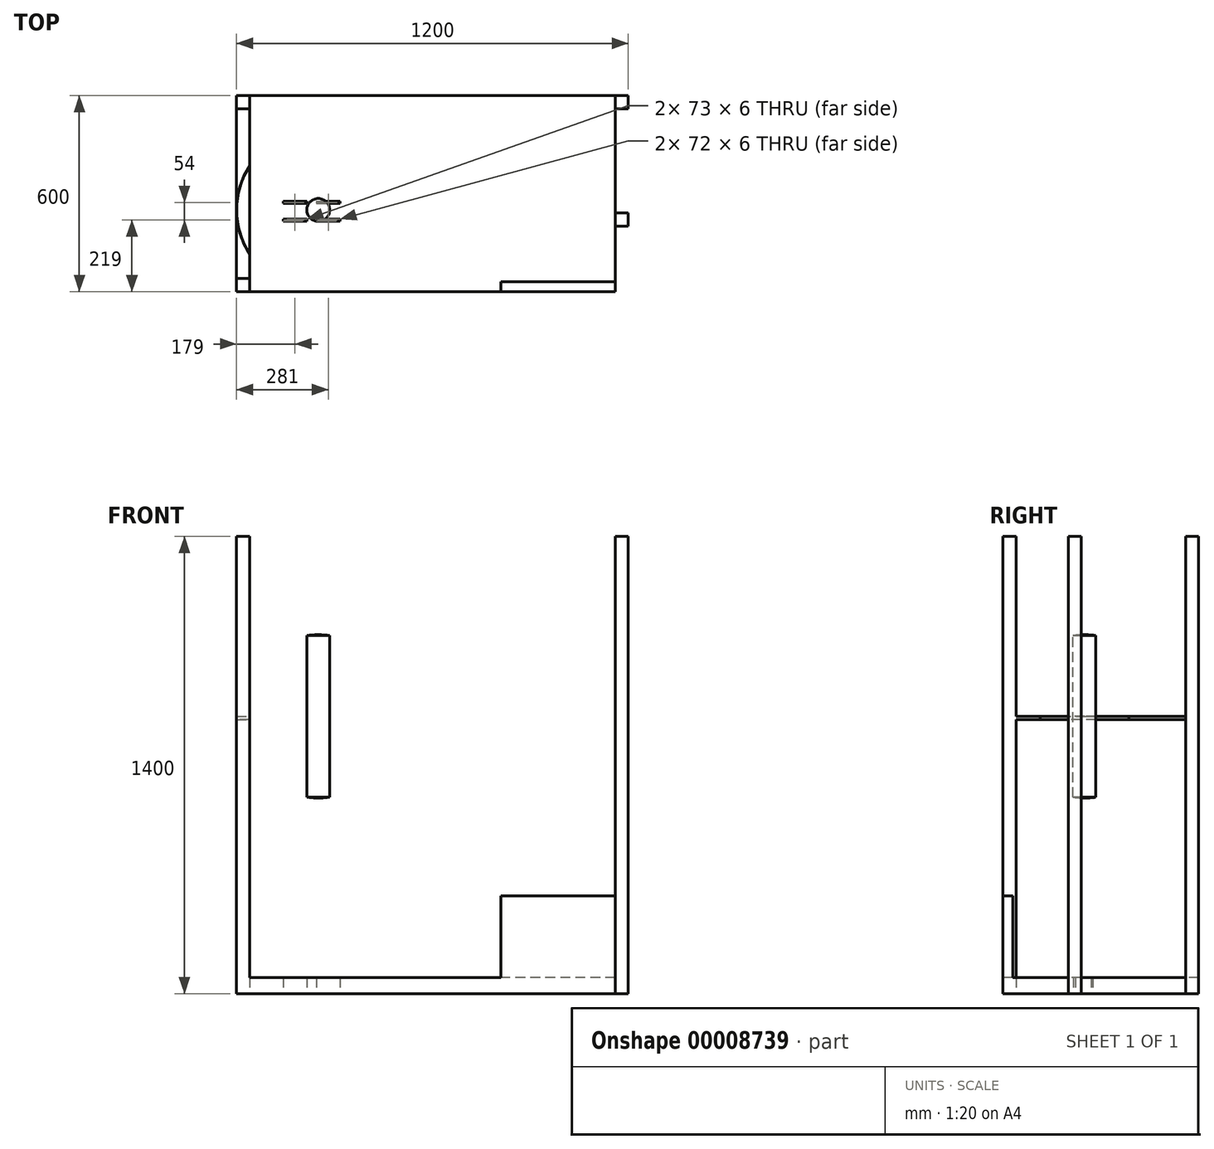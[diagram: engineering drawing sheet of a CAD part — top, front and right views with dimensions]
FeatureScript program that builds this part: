
annotation { "Feature Type Name" : "Feature", "Feature Type Description" : "" }
export const myFeature = defineFeature(function(context is Context, id is Id, definition is map)
    precondition{}
    {
        {
            var Q0;
            Q0=qCreatedBy(makeId("Top.planeOp"),FACE);
            var sketch = newSketch(context, id + "F0", { "sketchPlane" : qUnion([Q0])});
            skLineSegment(sketch, "E0.bottom", {"start": v(-250, 340) * mm, "end": v(870, 340) * mm});
            skLineSegment(sketch, "E0.top", {"start": v(-250, -260) * mm, "end": v(870, -260) * mm});
            skLineSegment(sketch, "E0.left", {"start": v(-250, 340) * mm, "end": v(-250, -260) * mm});
            skLineSegment(sketch, "E0.right", {"start": v(870, 340) * mm, "end": v(870, -260) * mm});
            skCircle(sketch, "E1", {"center": v(-40, 0) * mm, "radius": 250 * mm, "construction": true});
            skCircle(sketch, "E2", {"center": v(-40, 0) * mm, "radius": 30.5 * mm, "construction": true});
            skLineSegment(sketch, "E3", {"start": v(-250, 340) * mm, "end": v(870, -260) * mm, "construction": true});
            skLineSegment(sketch, "E4.left", {"start": v(-147.5, 16) * mm, "end": v(-147.5, 10) * mm});
            skLineSegment(sketch, "E4.right", {"start": v(-74.5, 16) * mm, "end": v(-74.5, 10) * mm});
            skLineSegment(sketch, "E5.top", {"start": v(-147.5, -44) * mm, "end": v(-74.5, -44) * mm});
            skLineSegment(sketch, "E5.left", {"start": v(-147.5, -38) * mm, "end": v(-147.5, -44) * mm});
            skLineSegment(sketch, "E5.right", {"start": v(-74.5, -38) * mm, "end": v(-74.5, -44) * mm});
            skLineSegment(sketch, "E6.bottom", {"start": v(-45, -38) * mm, "end": v(27, -38) * mm});
            skLineSegment(sketch, "E6.top", {"start": v(-45, -44) * mm, "end": v(27, -44) * mm});
            skLineSegment(sketch, "E6.left", {"start": v(-45, -38) * mm, "end": v(-45, -44) * mm});
            skLineSegment(sketch, "E6.right", {"start": v(27, -38) * mm, "end": v(27, -44) * mm});
            skLineSegment(sketch, "E7", {"start": v(-147.5, 16) * mm, "end": v(-74.5, 16) * mm});
            skLineSegment(sketch, "E8", {"start": v(-74.5, 10) * mm, "end": v(-147.5, 10) * mm});
            skLineSegment(sketch, "E9", {"start": v(-74.5, -38) * mm, "end": v(-147.5, -38) * mm});
            skLineSegment(sketch, "E10.bottom", {"start": v(-45, 16) * mm, "end": v(27, 16) * mm});
            skLineSegment(sketch, "E10.top", {"start": v(-45, 10) * mm, "end": v(27, 10) * mm});
            skLineSegment(sketch, "E10.left", {"start": v(-45, 16) * mm, "end": v(-45, 10) * mm});
            skLineSegment(sketch, "E10.right", {"start": v(27, 16) * mm, "end": v(27, 10) * mm});
            skLineSegment(sketch, "E11.bottom", {"start": v(870, -260) * mm, "end": v(520, -260) * mm, "construction": true});
            skLineSegment(sketch, "E11.top", {"start": v(870, -225) * mm, "end": v(520, -225) * mm, "construction": true});
            skLineSegment(sketch, "E11.left", {"start": v(870, -260) * mm, "end": v(870, -225) * mm, "construction": true});
            skLineSegment(sketch, "E11.right", {"start": v(520, -260) * mm, "end": v(520, -225) * mm, "construction": true});
            skSolve(sketch);
        }
        {
            var Q0;
            Q0 = qSketchRegion(id + "F0", true);
            extrude(context, id + "F1", {"entities" : qUnion([Q0]), "depth" : 49 * mm});
        }
        {
            var Q0;
            Q0=makeQuery(id+"F1.opExtrude","SWEPT_FACE",FACE,{"disambiguationData":[OSD([sQuery(id+"F0.wireOp",EDGE,"E0.top")])]});
            cPlane(context, id + "F2", {"entities" : qUnion([Q0]), "cplaneType" : CPlaneType.OFFSET, "offset" : 250 * mm, "oppositeDirection" : true, "width" : 150 * mm, "height" : 150 * mm});
        }
        {
            var Q0;
            Q0=makeQuery(id+"F1.opExtrude","CAP_FACE",FACE,{"disambiguationData":[OSD([sQuery(id+"F0.wireOp",EDGE,"E0.bottom"),sQuery(id+"F0.wireOp",EDGE,"E0.top"),sQuery(id+"F0.wireOp",EDGE,"E0.left"),sQuery(id+"F0.wireOp",EDGE,"E0.right"),sQuery(id+"F0.wireOp",EDGE,"E4.left"),sQuery(id+"F0.wireOp",EDGE,"E4.right"),sQuery(id+"F0.wireOp",EDGE,"E5.top"),sQuery(id+"F0.wireOp",EDGE,"E5.left"),sQuery(id+"F0.wireOp",EDGE,"E5.right"),sQuery(id+"F0.wireOp",EDGE,"E6.bottom"),sQuery(id+"F0.wireOp",EDGE,"E6.top"),sQuery(id+"F0.wireOp",EDGE,"E6.left"),sQuery(id+"F0.wireOp",EDGE,"E6.right"),sQuery(id+"F0.wireOp",EDGE,"E7"),sQuery(id+"F0.wireOp",EDGE,"E8"),sQuery(id+"F0.wireOp",EDGE,"E9"),sQuery(id+"F0.wireOp",EDGE,"E10.bottom"),sQuery(id+"F0.wireOp",EDGE,"E10.top"),sQuery(id+"F0.wireOp",EDGE,"E10.left"),sQuery(id+"F0.wireOp",EDGE,"E10.right"),sQuery(id+"F0.wireOp",EDGE,"473c598b-218d-4424-aa93-7a4d167d4974.bottom"),sQuery(id+"F0.wireOp",EDGE,"473c598b-218d-4424-aa93-7a4d167d4974.top"),sQuery(id+"F0.wireOp",EDGE,"473c598b-218d-4424-aa93-7a4d167d4974.left"),sQuery(id+"F0.wireOp",EDGE,"473c598b-218d-4424-aa93-7a4d167d4974.right"),sQuery(id+"F0.wireOp",EDGE,"ae9e9e06-8d92-4b63-a559-297d36669024.bottom"),sQuery(id+"F0.wireOp",EDGE,"ae9e9e06-8d92-4b63-a559-297d36669024.top"),sQuery(id+"F0.wireOp",EDGE,"ae9e9e06-8d92-4b63-a559-297d36669024.left"),sQuery(id+"F0.wireOp",EDGE,"ae9e9e06-8d92-4b63-a559-297d36669024.right"),sQuery(id+"F0.wireOp",EDGE,"cec4f3ce-f589-43ea-ba8f-dbbc267b80dc.bottom"),sQuery(id+"F0.wireOp",EDGE,"cec4f3ce-f589-43ea-ba8f-dbbc267b80dc.top"),sQuery(id+"F0.wireOp",EDGE,"cec4f3ce-f589-43ea-ba8f-dbbc267b80dc.left"),sQuery(id+"F0.wireOp",EDGE,"cec4f3ce-f589-43ea-ba8f-dbbc267b80dc.right"),sQuery(id+"F0.wireOp",EDGE,"411fdba1-57da-4452-b0fd-f241eb38766e.bottom"),sQuery(id+"F0.wireOp",EDGE,"411fdba1-57da-4452-b0fd-f241eb38766e.top"),sQuery(id+"F0.wireOp",EDGE,"411fdba1-57da-4452-b0fd-f241eb38766e.left"),sQuery(id+"F0.wireOp",EDGE,"411fdba1-57da-4452-b0fd-f241eb38766e.right")])],"isStart":true});
            var sketch = newSketch(context, id + "F3", { "sketchPlane" : qUnion([Q0])});
            skLineSegment(sketch, "E12.bottom", {"start": v(-250, 260) * mm, "end": v(-290, 260) * mm});
            skLineSegment(sketch, "E12.top", {"start": v(-250, 220) * mm, "end": v(-290, 220) * mm});
            skLineSegment(sketch, "E12.left", {"start": v(-250, 260) * mm, "end": v(-250, 220) * mm});
            skLineSegment(sketch, "E12.right", {"start": v(-290, 260) * mm, "end": v(-290, 220) * mm});
            skLineSegment(sketch, "E13.bottom", {"start": v(-250, -340) * mm, "end": v(-290, -340) * mm});
            skLineSegment(sketch, "E13.top", {"start": v(-250, -300) * mm, "end": v(-290, -300) * mm});
            skLineSegment(sketch, "E13.left", {"start": v(-250, -340) * mm, "end": v(-250, -300) * mm});
            skLineSegment(sketch, "E13.right", {"start": v(-290, -340) * mm, "end": v(-290, -300) * mm});
            skLineSegment(sketch, "E14.bottom", {"start": v(870, -340) * mm, "end": v(910, -340) * mm});
            skLineSegment(sketch, "E14.top", {"start": v(870, -300) * mm, "end": v(910, -300) * mm});
            skLineSegment(sketch, "E14.left", {"start": v(870, -340) * mm, "end": v(870, -300) * mm});
            skLineSegment(sketch, "E14.right", {"start": v(910, -340) * mm, "end": v(910, -300) * mm});
            skLineSegment(sketch, "E15.bottom", {"start": v(870, 19.56) * mm, "end": v(910, 19.56) * mm});
            skLineSegment(sketch, "E15.top", {"start": v(870, 59.56) * mm, "end": v(910, 59.56) * mm});
            skLineSegment(sketch, "E15.left", {"start": v(870, 19.56) * mm, "end": v(870, 59.56) * mm});
            skLineSegment(sketch, "E15.right", {"start": v(910, 19.56) * mm, "end": v(910, 59.56) * mm});
            skSolve(sketch);
        }
        {
            var Q0;
            Q0 = qSketchRegion(id + "F3", true);
            extrude(context, id + "F4", {"entities" : qUnion([Q0]), "operationType" : NewBodyOperationType.ADD, "oppositeDirection" : true, "depth" : 1400 * mm});
        }
        {
            var Q0;
            Q0=makeQuery(id+"F1.opExtrude","CAP_FACE",FACE,{"disambiguationData":[OSD([sQuery(id+"F0.wireOp",EDGE,"E0.bottom"),sQuery(id+"F0.wireOp",EDGE,"E0.top"),sQuery(id+"F0.wireOp",EDGE,"E0.left"),sQuery(id+"F0.wireOp",EDGE,"E0.right"),sQuery(id+"F0.wireOp",EDGE,"E4.left"),sQuery(id+"F0.wireOp",EDGE,"E4.right"),sQuery(id+"F0.wireOp",EDGE,"E5.top"),sQuery(id+"F0.wireOp",EDGE,"E5.left"),sQuery(id+"F0.wireOp",EDGE,"E5.right"),sQuery(id+"F0.wireOp",EDGE,"E6.bottom"),sQuery(id+"F0.wireOp",EDGE,"E6.top"),sQuery(id+"F0.wireOp",EDGE,"E6.left"),sQuery(id+"F0.wireOp",EDGE,"E6.right"),sQuery(id+"F0.wireOp",EDGE,"E7"),sQuery(id+"F0.wireOp",EDGE,"E8"),sQuery(id+"F0.wireOp",EDGE,"E9"),sQuery(id+"F0.wireOp",EDGE,"E10.bottom"),sQuery(id+"F0.wireOp",EDGE,"E10.top"),sQuery(id+"F0.wireOp",EDGE,"E10.left"),sQuery(id+"F0.wireOp",EDGE,"E10.right"),sQuery(id+"F0.wireOp",EDGE,"473c598b-218d-4424-aa93-7a4d167d4974.bottom"),sQuery(id+"F0.wireOp",EDGE,"473c598b-218d-4424-aa93-7a4d167d4974.top"),sQuery(id+"F0.wireOp",EDGE,"473c598b-218d-4424-aa93-7a4d167d4974.left"),sQuery(id+"F0.wireOp",EDGE,"473c598b-218d-4424-aa93-7a4d167d4974.right"),sQuery(id+"F0.wireOp",EDGE,"ae9e9e06-8d92-4b63-a559-297d36669024.bottom"),sQuery(id+"F0.wireOp",EDGE,"ae9e9e06-8d92-4b63-a559-297d36669024.top"),sQuery(id+"F0.wireOp",EDGE,"ae9e9e06-8d92-4b63-a559-297d36669024.left"),sQuery(id+"F0.wireOp",EDGE,"ae9e9e06-8d92-4b63-a559-297d36669024.right"),sQuery(id+"F0.wireOp",EDGE,"cec4f3ce-f589-43ea-ba8f-dbbc267b80dc.bottom"),sQuery(id+"F0.wireOp",EDGE,"cec4f3ce-f589-43ea-ba8f-dbbc267b80dc.top"),sQuery(id+"F0.wireOp",EDGE,"cec4f3ce-f589-43ea-ba8f-dbbc267b80dc.left"),sQuery(id+"F0.wireOp",EDGE,"cec4f3ce-f589-43ea-ba8f-dbbc267b80dc.right"),sQuery(id+"F0.wireOp",EDGE,"411fdba1-57da-4452-b0fd-f241eb38766e.bottom"),sQuery(id+"F0.wireOp",EDGE,"411fdba1-57da-4452-b0fd-f241eb38766e.top"),sQuery(id+"F0.wireOp",EDGE,"411fdba1-57da-4452-b0fd-f241eb38766e.left"),sQuery(id+"F0.wireOp",EDGE,"411fdba1-57da-4452-b0fd-f241eb38766e.right")])],"isStart":false});
            var sketch = newSketch(context, id + "F5", { "sketchPlane" : qUnion([Q0])});
            skLineSegment(sketch, "E16.bottom", {"start": v(870, -260) * mm, "end": v(520, -260) * mm});
            skLineSegment(sketch, "E16.top", {"start": v(870, -230) * mm, "end": v(520, -230) * mm});
            skLineSegment(sketch, "E16.left", {"start": v(870, -260) * mm, "end": v(870, -230) * mm});
            skLineSegment(sketch, "E16.right", {"start": v(520, -260) * mm, "end": v(520, -230) * mm});
            skSolve(sketch);
        }
        {
            var Q0;
            Q0 = qSketchRegion(id + "F5", true);
            extrude(context, id + "F6", {"entities" : qUnion([Q0]), "operationType" : NewBodyOperationType.ADD, "depth" : 250 * mm});
        }
        {
            var Q0;
            Q0=makeQuery(id+"F4.opExtrude","SWEPT_FACE",FACE,{"disambiguationData":[OSD([sQuery(id+"F3.wireOp",EDGE,"E13.top")])]});
            var sketch = newSketch(context, id + "F7", { "sketchPlane" : qUnion([Q0])});
            skLineSegment(sketch, "E17.bottom", {"start": v(-290, 849) * mm, "end": v(-250, 849) * mm});
            skLineSegment(sketch, "E17.top", {"start": v(-290, 839) * mm, "end": v(-250, 839) * mm});
            skLineSegment(sketch, "E17.left", {"start": v(-290, 849) * mm, "end": v(-290, 839) * mm});
            skLineSegment(sketch, "E17.right", {"start": v(-250, 849) * mm, "end": v(-250, 839) * mm});
            skSolve(sketch);
        }
        {
            var Q0;
            Q0 = qSketchRegion(id + "F7", true);
            var Q1;
            Q1 = qBodyType(qCreatedBy(id + "F7" ,EDGE), BodyType.WIRE);
            var Q2;
            Q2=makeQuery(id+"F4.opExtrude","SWEPT_FACE",FACE,{"disambiguationData":[OSD([sQuery(id+"F3.wireOp",EDGE,"E12.top")])]});
            extrude(context, id + "F8", {"entities" : qUnion([Q0]), "operationType" : NewBodyOperationType.ADD, "surfaceEntities" : qUnion([Q1]), "endBound" : BoundingType.UP_TO_SURFACE, "endBoundEntityFace" : qUnion([Q2]), "depth" : 25 * mm});
        }
        {
            var Q0;
            Q0=qCreatedBy(id+"F2.planeOp",FACE);
            var sketch = newSketch(context, id + "F9", { "sketchPlane" : qUnion([Q0])});
            skArc(sketch, "E18", {"start": v(210, 849) * mm, "mid": v(-40, 1099) * mm, "end": v(-290, 849) * mm});
            skLineSegment(sketch, "E19", {"start": v(-290, 849) * mm, "end": v(210, 849) * mm});
            skSolve(sketch);
        }
        {
            var Q0;
            Q0 = qSketchRegion(id + "F9", true);
            var Q1;
            Q1=sQuery(id+"F9.wireOp",EDGE,"E19");
            revolve(context, id + "F10", {"operationType" : NewBodyOperationType.ADD, "entities" : qUnion([Q0]), "axis" : qUnion([Q1]), "revolveType" : RevolveType.FULL});
        }
        {
            var Q0;
            {var subQ0=makeQuery(id+"F8.opExtrude","SWEPT_FACE",FACE,{"disambiguationData":[OSD([sQuery(id+"F7.wireOp",EDGE,"E17.bottom")])]});Q0=makeQuery(id+"F10.boolean.opBoolean","SPLIT",FACE,{"disambiguationData":[TD([makeQuery(id+"F4.opExtrude","SWEPT_FACE",FACE,{"disambiguationData":[OSD([sQuery(id+"F3.wireOp",EDGE,"E13.top")])]})])],"derivedFrom":subQ0});}
            var sketch = newSketch(context, id + "F11", { "sketchPlane" : qUnion([Q0])});
            skCircle(sketch, "E20", {"center": v(-40, -10) * mm, "radius": 35 * mm});
            skSolve(sketch);
        }
        {
            var Q0;
            Q0 = qSketchRegion(id + "F11", true);
            var Q1;
            Q1=makeQuery(id+"F10.opRevolve","SWEPT_FACE",FACE,{"disambiguationData":[OSD([sQuery(id+"F9.wireOp",EDGE,"E18")])]});
            extrude(context, id + "F12", {"entities" : qUnion([Q0]), "operationType" : NewBodyOperationType.REMOVE, "endBound" : BoundingType.UP_TO_SURFACE, "oppositeDirection" : true, "endBoundEntityFace" : qUnion([Q1]), "depth" : 25 * mm, "hasSecondDirection" : true, "secondDirectionOppositeDirection" : false, "secondDirectionDepth" : 500 * mm});
        }
    });
